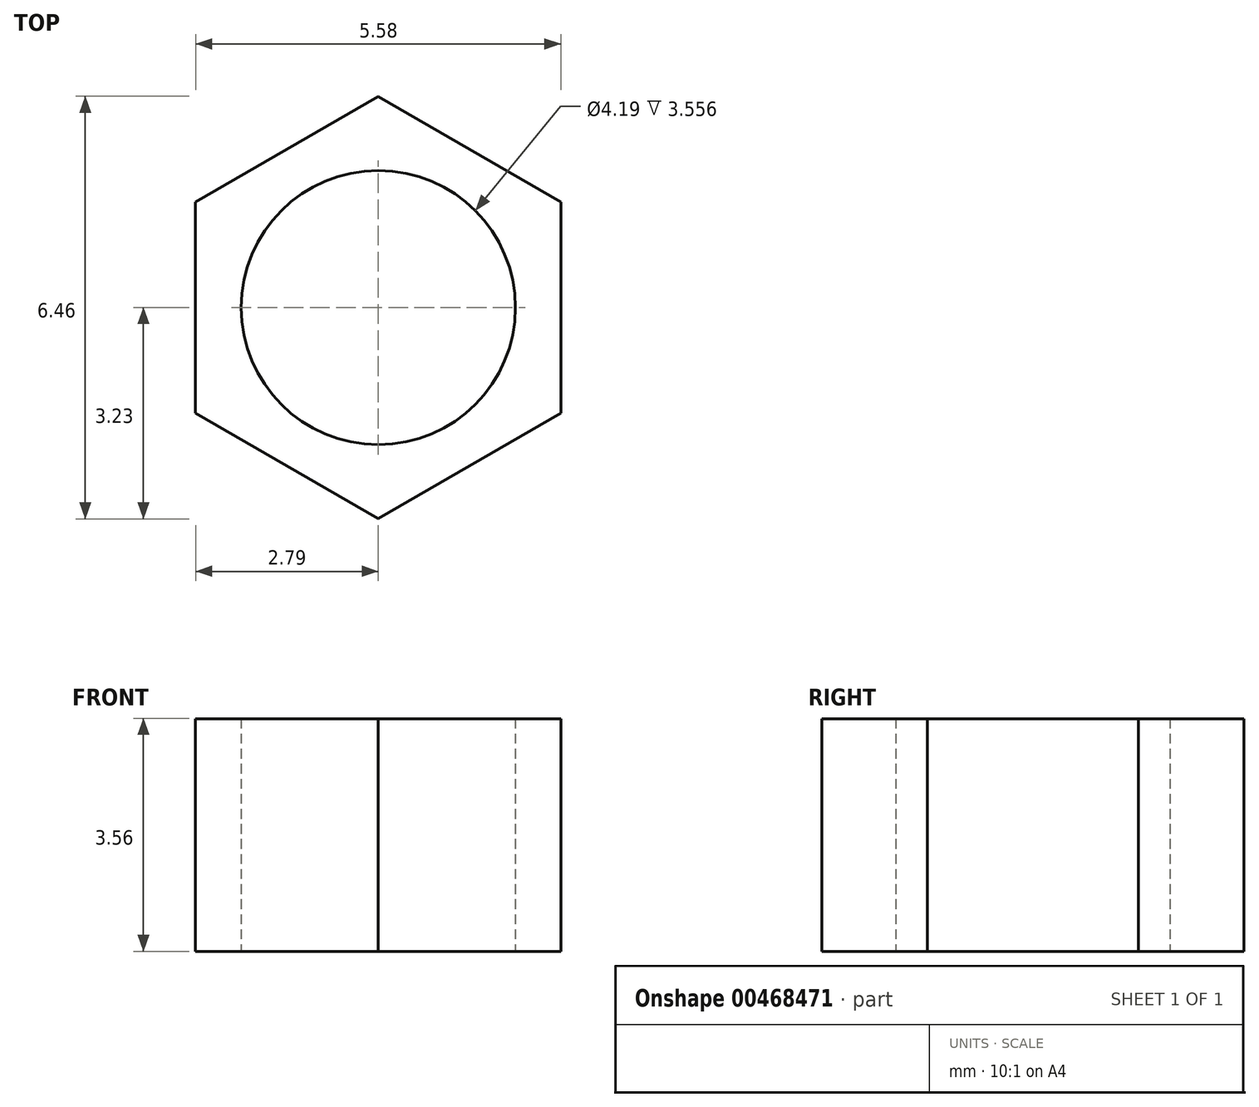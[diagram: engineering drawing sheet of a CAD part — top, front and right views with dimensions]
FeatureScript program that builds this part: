
annotation { "Feature Type Name" : "Feature", "Feature Type Description" : "" }
export const myFeature = defineFeature(function(context is Context, id is Id, definition is map)
    precondition{}
    {
        {
            var Q0;
            Q0=qCreatedBy(makeId("Top.planeOp"),FACE);
            var sketch = newSketch(context, id + "F0", { "sketchPlane" : qUnion([Q0])});
            skCircle(sketch, "E0.cCircle", {"center": v(0, 0) * mm, "radius": 2.8 * mm, "construction": true});
            skLineSegment(sketch, "E0.0", {"start": v(0, 3.23) * mm, "end": v(2.8, 1.61) * mm});
            skLineSegment(sketch, "E0.1", {"start": v(2.8, 1.61) * mm, "end": v(2.8, -1.61) * mm});
            skLineSegment(sketch, "E0.2", {"start": v(2.8, -1.61) * mm, "end": v(0, -3.23) * mm});
            skLineSegment(sketch, "E0.3", {"start": v(0, -3.23) * mm, "end": v(-2.8, -1.61) * mm});
            skLineSegment(sketch, "E0.4", {"start": v(-2.8, -1.61) * mm, "end": v(-2.8, 1.61) * mm});
            skLineSegment(sketch, "E0.5", {"start": v(-2.8, 1.61) * mm, "end": v(0, 3.23) * mm});
            skPoint(sketch, "E0.0.midPoint", {"position": v(1.4, 2.42) * mm});
            skCircle(sketch, "E1", {"center": v(0, 0) * mm, "radius": 2.1 * mm});
            skSolve(sketch);
        }
        {
            var Q0;
            Q0=makeQuery(id+"F0.imprint","IMPRINT",FACE,{"disambiguationData":[TD([[makeQuery(id+"F0.imprint","IMPRINT",EDGE,{"derivedFrom":sQuery(id+"F0.wireOp",EDGE,"E0.0")}),-1.0]])]});
            extrude(context, id + "F1", {"entities" : qUnion([Q0]), "depth" : 3.56 * mm});
        }
    });
